# Revit family: Haworth_Openest_SprigTable_Rectangle_AP_PRELIMINARY
name_source: partatom
category: Furniture
revit_build: Autodesk Revit 2018 (Build: 20170223_1515(x64)
units: mm (PartAtom-declared; Revit-internal decimal feet)

## family parameters
Always vertical = Yes
Cut with Voids When Loaded = No
OmniClass Number = 23.40.20.00
OmniClass Title = General Furniture and Specialties
Room Calculation Point = No
Shared = No
Work Plane-Based = No

## types (1)
- Rectangle
    Actual Depth = 510 mm  [stored 1.67323 ft]
    Actual Width = 1350 mm  [stored 4.42913 ft]
    Assembly Code = E2020200
    Description = Haworth - Openest - Sprig Table - Rectangle
    Height = 305 mm
    Manufacturer = Haworth
    Model = SEOSRX
    Revision No. = 1
    Size = Verify Final Dim. w/ Haworth
    Sustainability Info = https://www.haworth.com
    URL = https://www.haworth.com
    URL - Product = https://www.haworth.com
    Warranty = http://www.haworth.com

note: [stored X ft] marks values corroborated as IEEE doubles in the binary element streams (Revit-internal decimal feet)

## geometry (parser evidence)
native form markers: Sweep x3
no freeform markers — native parametric forms only
